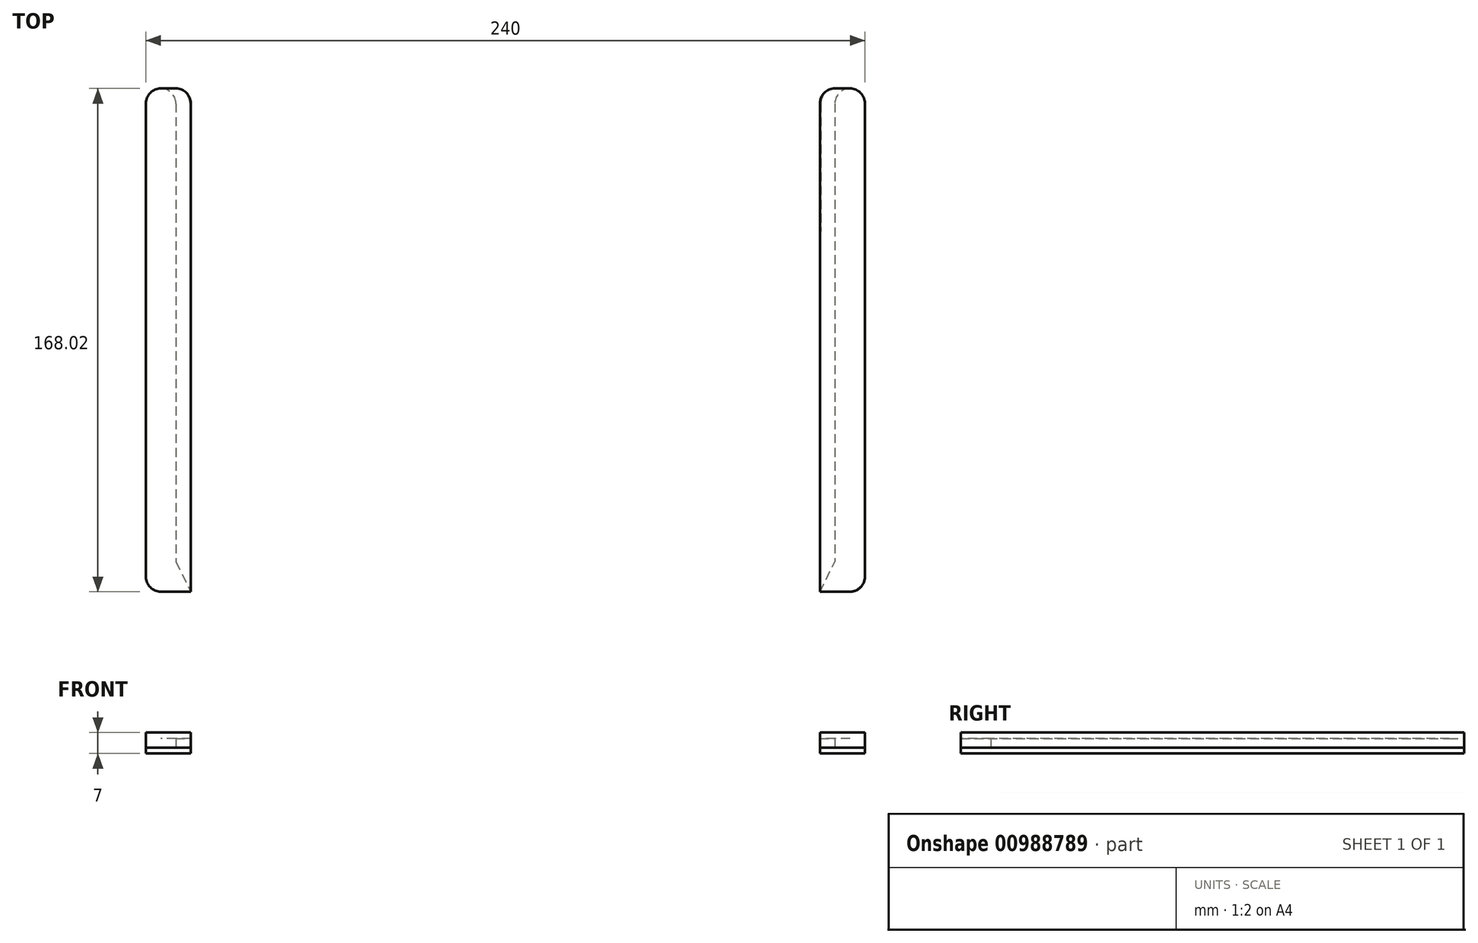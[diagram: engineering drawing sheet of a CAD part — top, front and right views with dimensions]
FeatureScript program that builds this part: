
annotation { "Feature Type Name" : "Feature", "Feature Type Description" : "" }
export const myFeature = defineFeature(function(context is Context, id is Id, definition is map)
    precondition{}
    {
        {
            var Q0;
            Q0=qCreatedBy(makeId("Top.planeOp"),FACE);
            var sketch = newSketch(context, id + "F0", { "sketchPlane" : qUnion([Q0])});
            skLineSegment(sketch, "E0.bottom", {"start": v(108, 77) * mm, "end": v(-108, 77) * mm});
            skLineSegment(sketch, "E0.top", {"start": v(108, -77) * mm, "end": v(-108, -77) * mm});
            skLineSegment(sketch, "E0.left", {"start": v(108, 77) * mm, "end": v(108, -77) * mm});
            skLineSegment(sketch, "E0.right", {"start": v(-108, 77) * mm, "end": v(-108, -77) * mm});
            skPoint(sketch, "E0.middle", {"position": v(0, 0) * mm});
            skLineSegment(sketch, "E1.bottom", {"start": v(110, 79) * mm, "end": v(-110, 79) * mm});
            skLineSegment(sketch, "E1.top", {"start": v(110, -79) * mm, "end": v(-110, -79) * mm});
            skLineSegment(sketch, "E1.left", {"start": v(110, 79) * mm, "end": v(110, -79) * mm});
            skLineSegment(sketch, "E1.right", {"start": v(-110, 79) * mm, "end": v(-110, -79) * mm});
            skLineSegment(sketch, "E2.bottom", {"start": v(-110, 79) * mm, "end": v(-120, 79) * mm});
            skLineSegment(sketch, "E2.top", {"start": v(-110, -79) * mm, "end": v(-120, -79) * mm});
            skLineSegment(sketch, "E2.right", {"start": v(-120, 79) * mm, "end": v(-120, -79) * mm});
            skLineSegment(sketch, "E3.bottom", {"start": v(110, 79) * mm, "end": v(120, 79) * mm});
            skLineSegment(sketch, "E3.top", {"start": v(110, -79) * mm, "end": v(120, -79) * mm});
            skLineSegment(sketch, "E3.right", {"start": v(120, 79) * mm, "end": v(120, -79) * mm});
            skLineSegment(sketch, "E4", {"start": v(120, -79) * mm, "end": v(115, -79) * mm});
            skLineSegment(sketch, "E5.bottom", {"start": v(120, -79) * mm, "end": v(105, -79) * mm});
            skLineSegment(sketch, "E5.top", {"start": v(120, -89) * mm, "end": v(105, -89) * mm});
            skLineSegment(sketch, "E5.left", {"start": v(120, -79) * mm, "end": v(120, -89) * mm});
            skLineSegment(sketch, "E5.right", {"start": v(105, -79) * mm, "end": v(105, -89) * mm});
            skLineSegment(sketch, "E6", {"start": v(105, -89) * mm, "end": v(110, -79) * mm});
            skLineSegment(sketch, "E7.bottom", {"start": v(-120, -79) * mm, "end": v(-105, -79) * mm});
            skLineSegment(sketch, "E7.top", {"start": v(-120, -89) * mm, "end": v(-105, -89) * mm});
            skLineSegment(sketch, "E7.left", {"start": v(-120, -79) * mm, "end": v(-120, -89) * mm});
            skLineSegment(sketch, "E7.right", {"start": v(-105, -79) * mm, "end": v(-105, -89) * mm});
            skLineSegment(sketch, "E8", {"start": v(-110, -79) * mm, "end": v(-105, -89) * mm});
            skSolve(sketch);
        }
        {
            var Q0;
            Q0=makeQuery(id+"F0.imprint","IMPRINT",FACE,{"disambiguationData":[TD([[makeQuery(id+"F0.imprint","IMPRINT",EDGE,{"derivedFrom":sQuery(id+"F0.wireOp",EDGE,"E2.bottom")}),1.0]])]});
            var Q1;
            Q1=makeQuery(id+"F0.imprint","IMPRINT",FACE,{"disambiguationData":[TD([[makeQuery(id+"F0.imprint","IMPRINT",EDGE,{"derivedFrom":sQuery(id+"F0.wireOp",EDGE,"E3.bottom")}),-1.0]])]});
            var Q2;
            {var subQ0=sQuery(id+"F0.wireOp",EDGE,"E3.top");Q2=makeQuery(id+"F0.imprint","IMPRINT",FACE,{"disambiguationData":[TD([[makeQuery(id+"F0.imprint","IMPRINT",EDGE,{"derivedFrom":subQ0}),-1.0]])]});}
            var Q3;
            {var subQ0=sQuery(id+"F0.wireOp",EDGE,"E3.top");Q3=makeQuery(id+"F0.imprint","IMPRINT",FACE,{"disambiguationData":[TD([[makeQuery(id+"F0.imprint","IMPRINT",EDGE,{"derivedFrom":subQ0}),1.0]])]});}
            var Q4;
            Q4=makeQuery(id+"F0.imprint","IMPRINT",FACE,{"disambiguationData":[TD([[makeQuery(id+"F0.imprint","IMPRINT",EDGE,{"derivedFrom":sQuery(id+"F0.wireOp",EDGE,"E5.top")}),-1.0]])]});
            var Q5;
            Q5=makeQuery(id+"F0.imprint","IMPRINT",FACE,{"disambiguationData":[TD([[makeQuery(id+"F0.imprint","IMPRINT",EDGE,{"derivedFrom":sQuery(id+"F0.wireOp",EDGE,"E7.top")}),1.0]])]});
            extrude(context, id + "F1", {"entities" : qUnion([Q0, Q1, Q2, Q3, Q4, Q5]), "depth" : 3 * mm, "offsetDistance" : 25 * mm});
        }
        {
            var Q0;
            Q0=makeQuery(id+"F1.opExtrude","CAP_FACE",FACE,{"disambiguationData":[OSD([sQuery(id+"F0.wireOp",EDGE,"E2.bottom"),sQuery(id+"F0.wireOp",EDGE,"E1.right"),sQuery(id+"F0.wireOp",EDGE,"E2.right"),sQuery(id+"F0.wireOp",EDGE,"E7.top"),sQuery(id+"F0.wireOp",EDGE,"E7.left"),sQuery(id+"F0.wireOp",EDGE,"E8")])],"isStart":false});
            var sketch = newSketch(context, id + "F2", { "sketchPlane" : qUnion([Q0])});
            skLineSegment(sketch, "E9.bottom", {"start": v(-120, -89) * mm, "end": v(-105, -89) * mm});
            skLineSegment(sketch, "E9.top", {"start": v(-120, 79) * mm, "end": v(-105, 79) * mm});
            skLineSegment(sketch, "E9.left", {"start": v(-120, -89) * mm, "end": v(-120, 79) * mm});
            skLineSegment(sketch, "E9.right", {"start": v(-105, -89) * mm, "end": v(-105, 79) * mm});
            skSolve(sketch);
        }
        {
            var Q0;
            {var subQ2=sQuery(id+"F2.wireOp",EDGE,"E9.right");Q0=makeQuery(id+"F2.imprint","IMPRINT",FACE,{"disambiguationData":[TD([[makeQuery(id+"F2.imprint","IMPRINT",EDGE,{"derivedFrom":subQ2}),1.0]])]});}
            var Q1;
            Q1=makeQuery(id+"F2.imprint","IMPRINT",FACE,{"disambiguationData":[TD([[makeQuery(id+"F2.imprint","IMPRINT",EDGE,{"derivedFrom":sQuery(id+"F2.wireOp",EDGE,"E9.bottom")}),1.0]])]});
            extrude(context, id + "F3", {"entities" : qUnion([Q0, Q1]), "operationType" : NewBodyOperationType.ADD, "depth" : 2 * mm, "offsetDistance" : 25 * mm});
        }
        {
            var Q0;
            Q0=makeQuery(id+"F1.opExtrude","CAP_FACE",FACE,{"disambiguationData":[OSD([sQuery(id+"F0.wireOp",EDGE,"E3.bottom"),sQuery(id+"F0.wireOp",EDGE,"E1.left"),sQuery(id+"F0.wireOp",EDGE,"E3.right"),sQuery(id+"F0.wireOp",EDGE,"E5.top"),sQuery(id+"F0.wireOp",EDGE,"E5.left"),sQuery(id+"F0.wireOp",EDGE,"E6")])],"isStart":false});
            var sketch = newSketch(context, id + "F4", { "sketchPlane" : qUnion([Q0])});
            skLineSegment(sketch, "E10.bottom", {"start": v(120, -89) * mm, "end": v(105, -89) * mm});
            skLineSegment(sketch, "E10.top", {"start": v(120, 79) * mm, "end": v(105, 79) * mm});
            skLineSegment(sketch, "E10.left", {"start": v(120, -89) * mm, "end": v(120, 79) * mm});
            skLineSegment(sketch, "E10.right", {"start": v(105, -89) * mm, "end": v(105, 79) * mm});
            skSolve(sketch);
        }
        {
            var Q0;
            {var subQ2=sQuery(id+"F4.wireOp",EDGE,"E10.right");Q0=makeQuery(id+"F4.imprint","IMPRINT",FACE,{"disambiguationData":[TD([[makeQuery(id+"F4.imprint","IMPRINT",EDGE,{"derivedFrom":subQ2}),-1.0]])]});}
            var Q1;
            Q1=makeQuery(id+"F4.imprint","IMPRINT",FACE,{"disambiguationData":[TD([[makeQuery(id+"F4.imprint","IMPRINT",EDGE,{"derivedFrom":sQuery(id+"F4.wireOp",EDGE,"E10.bottom")}),-1.0]])]});
            extrude(context, id + "F5", {"entities" : qUnion([Q0, Q1]), "operationType" : NewBodyOperationType.ADD, "depth" : 2 * mm, "offsetDistance" : 25 * mm});
        }
        {
            var Q0;
            Q0=makeQuery(id+"F3.opExtrude","SWEPT_EDGE",EDGE,{"disambiguationData":[OSD([sQuery(id+"F2.wireOp",EDGE,"E9.top"),sQuery(id+"F2.wireOp",EDGE,"E9.right")])]});
            var Q1;
            Q1=makeQuery(id+"F5.opExtrude","SWEPT_EDGE",EDGE,{"disambiguationData":[OSD([sQuery(id+"F4.wireOp",EDGE,"E10.top"),sQuery(id+"F4.wireOp",EDGE,"E10.right")])]});
            fillet(context, id + "F6", {"entities" : qUnion([Q0, Q1]), "radius" : 5 * mm, "tangentPropagation" : true, "allowEdgeOverflow" : false});
        }
        {
            var Q0;
            Q0=makeQuery(id+"F5.boolean.opBoolean","MERGE",EDGE,{"derivedFrom":[makeQuery(id+"F1.opExtrude","SWEPT_EDGE",EDGE,{"disambiguationData":[OSD([sQuery(id+"F0.wireOp",EDGE,"E3.bottom"),sQuery(id+"F0.wireOp",EDGE,"E3.right")])]}),makeQuery(id+"F5.opExtrude","SWEPT_EDGE",EDGE,{"disambiguationData":[OSD([sQuery(id+"F4.wireOp",EDGE,"E10.top"),sQuery(id+"F4.wireOp",EDGE,"E10.left")])]})]});
            var Q1;
            Q1=makeQuery(id+"F5.boolean.opBoolean","MERGE",EDGE,{"derivedFrom":[makeQuery(id+"F1.opExtrude","SWEPT_EDGE",EDGE,{"disambiguationData":[OSD([sQuery(id+"F0.wireOp",EDGE,"E5.top"),sQuery(id+"F0.wireOp",EDGE,"E5.left")])]}),makeQuery(id+"F5.opExtrude","SWEPT_EDGE",EDGE,{"disambiguationData":[OSD([sQuery(id+"F4.wireOp",EDGE,"E10.bottom"),sQuery(id+"F4.wireOp",EDGE,"E10.left")])]})]});
            var Q2;
            Q2=makeQuery(id+"F3.boolean.opBoolean","MERGE",EDGE,{"derivedFrom":[makeQuery(id+"F1.opExtrude","SWEPT_EDGE",EDGE,{"disambiguationData":[OSD([sQuery(id+"F0.wireOp",EDGE,"E7.top"),sQuery(id+"F0.wireOp",EDGE,"E7.left")])]}),makeQuery(id+"F3.opExtrude","SWEPT_EDGE",EDGE,{"disambiguationData":[OSD([sQuery(id+"F2.wireOp",EDGE,"E9.bottom"),sQuery(id+"F2.wireOp",EDGE,"E9.left")])]})]});
            var Q3;
            Q3=makeQuery(id+"F3.boolean.opBoolean","MERGE",EDGE,{"derivedFrom":[makeQuery(id+"F1.opExtrude","SWEPT_EDGE",EDGE,{"disambiguationData":[OSD([sQuery(id+"F0.wireOp",EDGE,"E2.bottom"),sQuery(id+"F0.wireOp",EDGE,"E2.right")])]}),makeQuery(id+"F3.opExtrude","SWEPT_EDGE",EDGE,{"disambiguationData":[OSD([sQuery(id+"F2.wireOp",EDGE,"E9.top"),sQuery(id+"F2.wireOp",EDGE,"E9.left")])]})]});
            fillet(context, id + "F7", {"entities" : qUnion([Q0, Q1, Q2, Q3]), "radius" : 5 * mm, "tangentPropagation" : true, "allowEdgeOverflow" : false});
        }
        {
            var Q0;
            Q0=makeQuery(id+"F1.opExtrude","SWEPT_EDGE",EDGE,{"disambiguationData":[OSD([sQuery(id+"F0.wireOp",EDGE,"E1.bottom"),sQuery(id+"F0.wireOp",EDGE,"E3.bottom"),sQuery(id+"F0.wireOp",EDGE,"E1.left")])]});
            var Q1;
            Q1=makeQuery(id+"F1.opExtrude","SWEPT_EDGE",EDGE,{"disambiguationData":[OSD([sQuery(id+"F0.wireOp",EDGE,"E1.bottom"),sQuery(id+"F0.wireOp",EDGE,"E2.bottom"),sQuery(id+"F0.wireOp",EDGE,"E1.right")])]});
            fillet(context, id + "F8", {"entities" : qUnion([Q0, Q1]), "radius" : 5 * mm, "tangentPropagation" : true, "allowEdgeOverflow" : false});
        }
        {
            var Q0;
            Q0=makeQuery(id+"F1.opExtrude","CAP_FACE",FACE,{"disambiguationData":[OSD([sQuery(id+"F0.wireOp",EDGE,"E2.bottom"),sQuery(id+"F0.wireOp",EDGE,"E1.right"),sQuery(id+"F0.wireOp",EDGE,"E2.right"),sQuery(id+"F0.wireOp",EDGE,"E7.top"),sQuery(id+"F0.wireOp",EDGE,"E7.left"),sQuery(id+"F0.wireOp",EDGE,"E8")])],"isStart":true});
            var sketch = newSketch(context, id + "F9", { "sketchPlane" : qUnion([Q0])});
            skLineSegment(sketch, "E11", {"start": v(-120, -79) * mm, "end": v(-105.3, -79) * mm});
            skLineSegment(sketch, "E12", {"start": v(-105.3, -79) * mm, "end": v(-105, 89) * mm});
            skLineSegment(sketch, "E13", {"start": v(-105, 89) * mm, "end": v(-120, 89.03) * mm});
            skLineSegment(sketch, "E14", {"start": v(-120, 89.03) * mm, "end": v(-120, -79) * mm});
            skLineSegment(sketch, "E15.MirrorCS", {"start": v(105.3, -79) * mm, "end": v(105, 89) * mm});
            skLineSegment(sketch, "E16.MirrorCS", {"start": v(105, 89) * mm, "end": v(120, 89.03) * mm});
            skLineSegment(sketch, "E17.MirrorCS", {"start": v(120, 89.03) * mm, "end": v(120, -79) * mm});
            skLineSegment(sketch, "E18.MirrorCS", {"start": v(120, -79) * mm, "end": v(105.3, -79) * mm});
            skSolve(sketch);
        }
        {
            var Q0;
            {var subQ0=sQuery(id+"F0.wireOp",EDGE,"E8");Q0=makeQuery(id+"F9.imprint","IMPRINT",FACE,{"disambiguationData":[TD([[makeQuery(id+"F9.imprint","IMPRINT",EDGE,{"derivedFrom":makeQuery(id+"F1.opExtrude","CAP_EDGE",EDGE,{"disambiguationData":[OSD([subQ0])],"isStart":true})}),1.0]])]});}
            var Q1;
            {var subQ6=sQuery(id+"F9.wireOp",EDGE,"E12");Q1=makeQuery(id+"F9.imprint","IMPRINT",FACE,{"disambiguationData":[TD([[makeQuery(id+"F9.imprint","IMPRINT",EDGE,{"derivedFrom":subQ6}),1.0]])]});}
            var Q2;
            Q2=makeQuery(id+"F9.imprint","IMPRINT",FACE,{"disambiguationData":[TD([[makeQuery(id+"F9.imprint","IMPRINT",EDGE,{"derivedFrom":sQuery(id+"F9.wireOp",EDGE,"E15.MirrorCS")}),-1.0]])]});
            extrude(context, id + "F10", {"entities" : qUnion([Q0, Q1, Q2]), "depth" : 2 * mm, "offsetDistance" : 25 * mm});
        }
        {
            var Q0;
            Q0=makeQuery(id+"F10.opExtrude","SWEPT_EDGE",EDGE,{"disambiguationData":[OSD([sQuery(id+"F9.wireOp",EDGE,"E11"),sQuery(id+"F9.wireOp",EDGE,"E12")])]});
            var Q1;
            Q1=makeQuery(id+"F10.opExtrude","SWEPT_EDGE",EDGE,{"disambiguationData":[OSD([sQuery(id+"F9.wireOp",EDGE,"E17.MirrorCS"),sQuery(id+"F9.wireOp",EDGE,"E18.MirrorCS")])]});
            var Q2;
            Q2=makeQuery(id+"F10.opExtrude","SWEPT_EDGE",EDGE,{"disambiguationData":[OSD([sQuery(id+"F9.wireOp",EDGE,"E15.MirrorCS"),sQuery(id+"F9.wireOp",EDGE,"E18.MirrorCS")])]});
            var Q3;
            Q3=makeQuery(id+"F10.opExtrude","SWEPT_EDGE",EDGE,{"disambiguationData":[OSD([sQuery(id+"F9.wireOp",EDGE,"E16.MirrorCS"),sQuery(id+"F9.wireOp",EDGE,"E17.MirrorCS")])]});
            fillet(context, id + "F11", {"entities" : qUnion([Q0, Q1, Q2, Q3]), "radius" : 5 * mm, "tangentPropagation" : true, "allowEdgeOverflow" : false});
        }
    });
